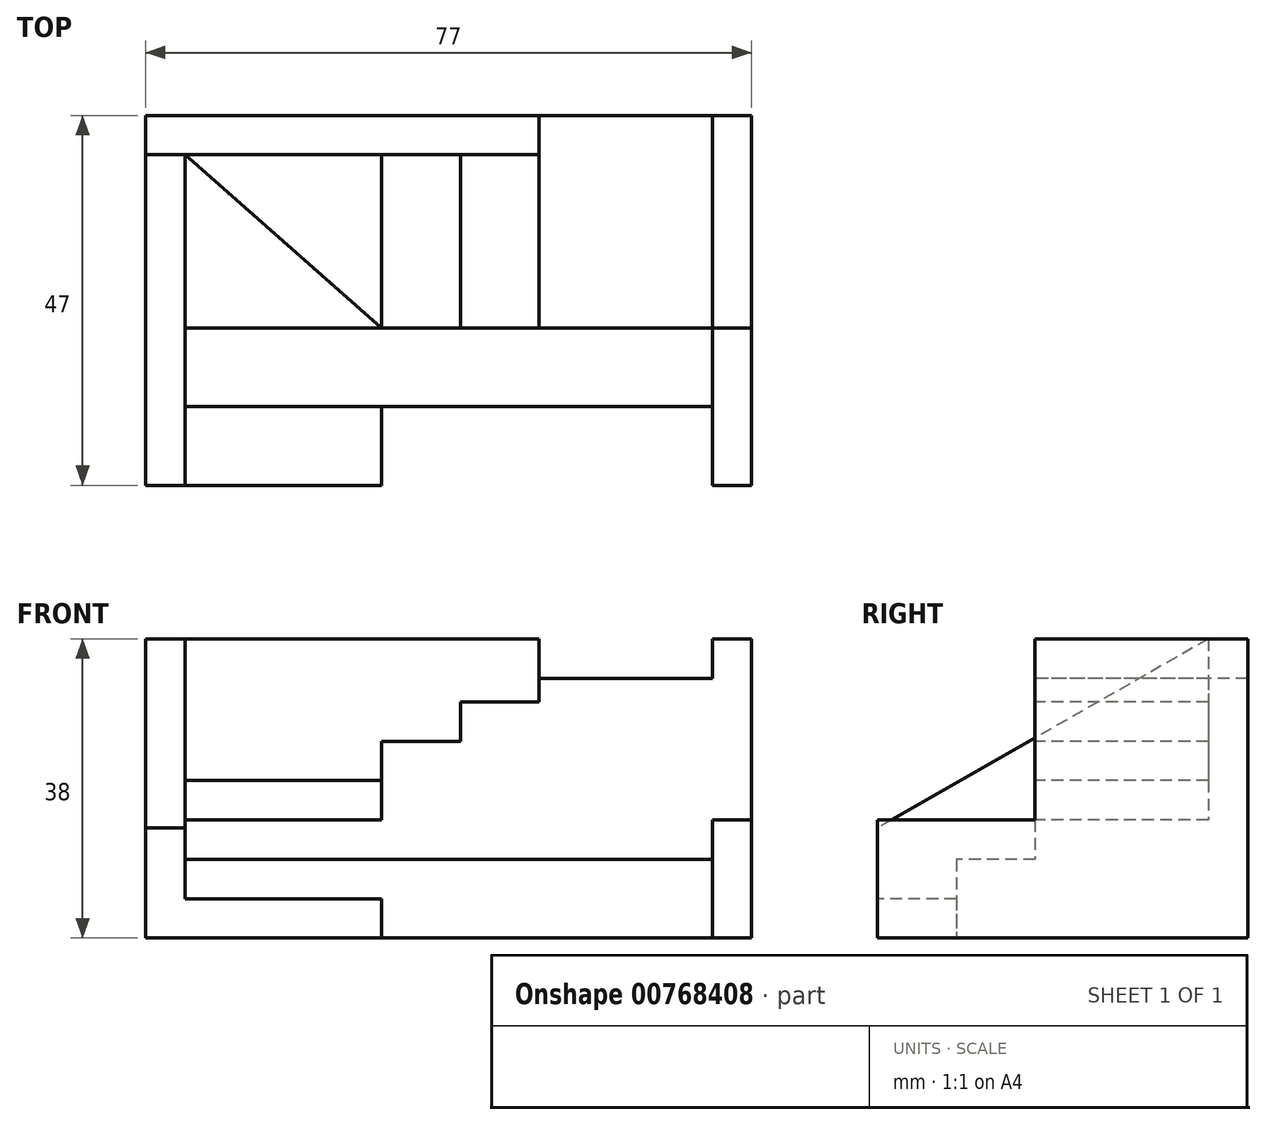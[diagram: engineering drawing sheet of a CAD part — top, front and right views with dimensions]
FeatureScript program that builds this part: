
annotation { "Feature Type Name" : "Feature", "Feature Type Description" : "" }
export const myFeature = defineFeature(function(context is Context, id is Id, definition is map)
    precondition{}
    {
        {
            var Q0;
            Q0=qCreatedBy(makeId("Top.planeOp"),FACE);
            var sketch = newSketch(context, id + "F0", { "sketchPlane" : qUnion([Q0])});
            skLineSegment(sketch, "E0.bottom", {"start": v(-50, 23.88) * mm, "end": v(27, 23.88) * mm});
            skLineSegment(sketch, "E0.top", {"start": v(-50, -23.12) * mm, "end": v(-20, -23.12) * mm});
            skLineSegment(sketch, "E0.left", {"start": v(-50, 23.88) * mm, "end": v(-50, -23.12) * mm});
            skLineSegment(sketch, "E0.right", {"start": v(27, 23.88) * mm, "end": v(27, -23.12) * mm});
            skLineSegment(sketch, "E1", {"start": v(-45, 18.88) * mm, "end": v(-45, -23.12) * mm});
            skLineSegment(sketch, "E2", {"start": v(-50, 18.88) * mm, "end": v(0, 18.88) * mm});
            skLineSegment(sketch, "E3", {"start": v(-45, -13.12) * mm, "end": v(22, -13.12) * mm});
            skLineSegment(sketch, "E4", {"start": v(-45, -3.12) * mm, "end": v(27, -3.12) * mm});
            skLineSegment(sketch, "E5", {"start": v(-20, 18.88) * mm, "end": v(-20, -3.12) * mm});
            skLineSegment(sketch, "E6", {"start": v(-45, 18.88) * mm, "end": v(-20, -3.12) * mm});
            skLineSegment(sketch, "E7", {"start": v(-10, 18.88) * mm, "end": v(-10, -3.12) * mm});
            skLineSegment(sketch, "E8", {"start": v(0, 18.88) * mm, "end": v(0, -3.12) * mm});
            skLineSegment(sketch, "E9", {"start": v(0, 18.88) * mm, "end": v(0, 23.88) * mm});
            skLineSegment(sketch, "E10", {"start": v(22, 23.88) * mm, "end": v(22, -23.12) * mm});
            skLineSegment(sketch, "E11", {"start": v(-20, -23.12) * mm, "end": v(-20, -13.12) * mm});
            skLineSegment(sketch, "E12.trimOffspring", {"start": v(22, -23.12) * mm, "end": v(27, -23.12) * mm});
            skSolve(sketch);
        }
        {
            var Q0;
            {var subQ5=sQuery(id+"F0.wireOp",EDGE,"E0.left");var subQ6=sQuery(id+"F0.wireOp",EDGE,"E0.top");var subQ7=makeQuery(id+"F0.imprint","INTERSECT",VERTEX,{"derivedFrom":[subQ6,subQ5]});Q0=makeQuery(id+"F0.imprint","IMPRINT",FACE,{"disambiguationData":[TD([[makeQuery(id+"F0.imprint","IMPRINT",EDGE,{"disambiguationData":[TD([[subQ7,-1.0]])],"derivedFrom":subQ6}),1.0]])]});}
            extrude(context, id + "F1", {"entities" : qUnion([Q0]), "depth" : 38 * mm, "offsetDistance" : 25 * mm});
        }
        {
            var Q0;
            Q0=makeQuery(id+"F1.opExtrude","SWEPT_FACE",FACE,{"disambiguationData":[OSD([sQuery(id+"F0.wireOp",EDGE,"E1")])]});
            var sketch = newSketch(context, id + "F2", { "sketchPlane" : qUnion([Q0])});
            skLineSegment(sketch, "E13", {"start": v(18.88, 38) * mm, "end": v(-23.12, 14) * mm});
            skSolve(sketch);
        }
        {
            var Q0;
            {var subQ0=sQuery(id+"F2.wireOp",EDGE,"E13");Q0=makeQuery(id+"F2.imprint","IMPRINT",FACE,{"disambiguationData":[TD([[makeQuery(id+"F2.imprint","IMPRINT",EDGE,{"derivedFrom":subQ0}),-1.0]])]});}
            extrude(context, id + "F3", {"entities" : qUnion([Q0]), "operationType" : NewBodyOperationType.REMOVE, "oppositeDirection" : true, "depth" : 25 * mm, "offsetDistance" : 25 * mm});
        }
        {
            var Q0;
            {var subQ7=sQuery(id+"F0.wireOp",EDGE,"E9");Q0=makeQuery(id+"F0.imprint","IMPRINT",FACE,{"disambiguationData":[TD([[makeQuery(id+"F0.imprint","IMPRINT",EDGE,{"derivedFrom":subQ7}),1.0]])]});}
            extrude(context, id + "F4", {"entities" : qUnion([Q0]), "operationType" : NewBodyOperationType.ADD, "depth" : 38 * mm, "offsetDistance" : 25 * mm});
        }
        {
            var Q0;
            {var subQ0=sQuery(id+"F0.wireOp",EDGE,"E11");Q0=makeQuery(id+"F0.imprint","IMPRINT",FACE,{"disambiguationData":[TD([[makeQuery(id+"F0.imprint","IMPRINT",EDGE,{"derivedFrom":subQ0}),1.0]])]});}
            extrude(context, id + "F5", {"entities" : qUnion([Q0]), "operationType" : NewBodyOperationType.ADD, "depth" : 5 * mm, "offsetDistance" : 25 * mm});
        }
        {
            var Q0;
            {var subQ1=sQuery(id+"F0.wireOp",EDGE,"E1");var subQ5=sQuery(id+"F0.wireOp",EDGE,"E3");var subQ9=makeQuery(id+"F0.imprint","INTERSECT",VERTEX,{"derivedFrom":[subQ1,subQ5]});Q0=makeQuery(id+"F0.imprint","IMPRINT",FACE,{"disambiguationData":[TD([[makeQuery(id+"F0.imprint","IMPRINT",EDGE,{"disambiguationData":[TD([[subQ9,1.0]])],"derivedFrom":subQ1}),1.0]])]});}
            extrude(context, id + "F6", {"entities" : qUnion([Q0]), "operationType" : NewBodyOperationType.ADD, "depth" : 10 * mm, "offsetDistance" : 25 * mm});
        }
        {
            var Q0;
            {var subQ2=sQuery(id+"F0.wireOp",EDGE,"E12.trimOffspring");Q0=makeQuery(id+"F0.imprint","IMPRINT",FACE,{"disambiguationData":[TD([[makeQuery(id+"F0.imprint","IMPRINT",EDGE,{"derivedFrom":subQ2}),1.0]])]});}
            extrude(context, id + "F7", {"entities" : qUnion([Q0]), "operationType" : NewBodyOperationType.ADD, "depth" : 15 * mm, "offsetDistance" : 25 * mm});
        }
        {
            var Q0;
            {var subQ0=sQuery(id+"F0.wireOp",EDGE,"E0.right");var subQ1=sQuery(id+"F0.wireOp",EDGE,"E0.bottom");var subQ2=makeQuery(id+"F0.imprint","INTERSECT",VERTEX,{"derivedFrom":[subQ1,subQ0]});Q0=makeQuery(id+"F0.imprint","IMPRINT",FACE,{"disambiguationData":[TD([[makeQuery(id+"F0.imprint","IMPRINT",EDGE,{"disambiguationData":[TD([[subQ2,1.0]])],"derivedFrom":subQ1}),-1.0]])]});}
            extrude(context, id + "F8", {"entities" : qUnion([Q0]), "operationType" : NewBodyOperationType.ADD, "depth" : 38 * mm, "offsetDistance" : 25 * mm});
        }
        {
            var Q0;
            {var subQ1=sQuery(id+"F0.wireOp",EDGE,"E8");Q0=makeQuery(id+"F0.imprint","IMPRINT",FACE,{"disambiguationData":[TD([[makeQuery(id+"F0.imprint","IMPRINT",EDGE,{"derivedFrom":subQ1}),1.0]])]});}
            extrude(context, id + "F9", {"entities" : qUnion([Q0]), "operationType" : NewBodyOperationType.ADD, "depth" : 33 * mm, "offsetDistance" : 25 * mm});
        }
        {
            var Q0;
            {var subQ0=sQuery(id+"F0.wireOp",EDGE,"E6");Q0=makeQuery(id+"F0.imprint","IMPRINT",FACE,{"disambiguationData":[TD([[makeQuery(id+"F0.imprint","IMPRINT",EDGE,{"derivedFrom":subQ0}),-1.0]])]});}
            extrude(context, id + "F10", {"entities" : qUnion([Q0]), "operationType" : NewBodyOperationType.ADD, "depth" : 15 * mm, "offsetDistance" : 25 * mm});
        }
        {
            var Q0;
            {var subQ2=sQuery(id+"F0.wireOp",EDGE,"E5");Q0=makeQuery(id+"F0.imprint","IMPRINT",FACE,{"disambiguationData":[TD([[makeQuery(id+"F0.imprint","IMPRINT",EDGE,{"derivedFrom":subQ2}),-1.0]])]});}
            extrude(context, id + "F11", {"entities" : qUnion([Q0]), "operationType" : NewBodyOperationType.ADD, "depth" : 20 * mm, "offsetDistance" : 25 * mm});
        }
        {
            var Q0;
            {var subQ0=sQuery(id+"F0.wireOp",EDGE,"E5");Q0=makeQuery(id+"F0.imprint","IMPRINT",FACE,{"disambiguationData":[TD([[makeQuery(id+"F0.imprint","IMPRINT",EDGE,{"derivedFrom":subQ0}),1.0]])]});}
            extrude(context, id + "F12", {"entities" : qUnion([Q0]), "operationType" : NewBodyOperationType.ADD, "depth" : 25 * mm, "offsetDistance" : 25 * mm});
        }
        {
            var Q0;
            {var subQ2=sQuery(id+"F0.wireOp",EDGE,"E7");Q0=makeQuery(id+"F0.imprint","IMPRINT",FACE,{"disambiguationData":[TD([[makeQuery(id+"F0.imprint","IMPRINT",EDGE,{"derivedFrom":subQ2}),1.0]])]});}
            extrude(context, id + "F13", {"entities" : qUnion([Q0]), "operationType" : NewBodyOperationType.ADD, "depth" : 30 * mm, "offsetDistance" : 25 * mm});
        }
    });
